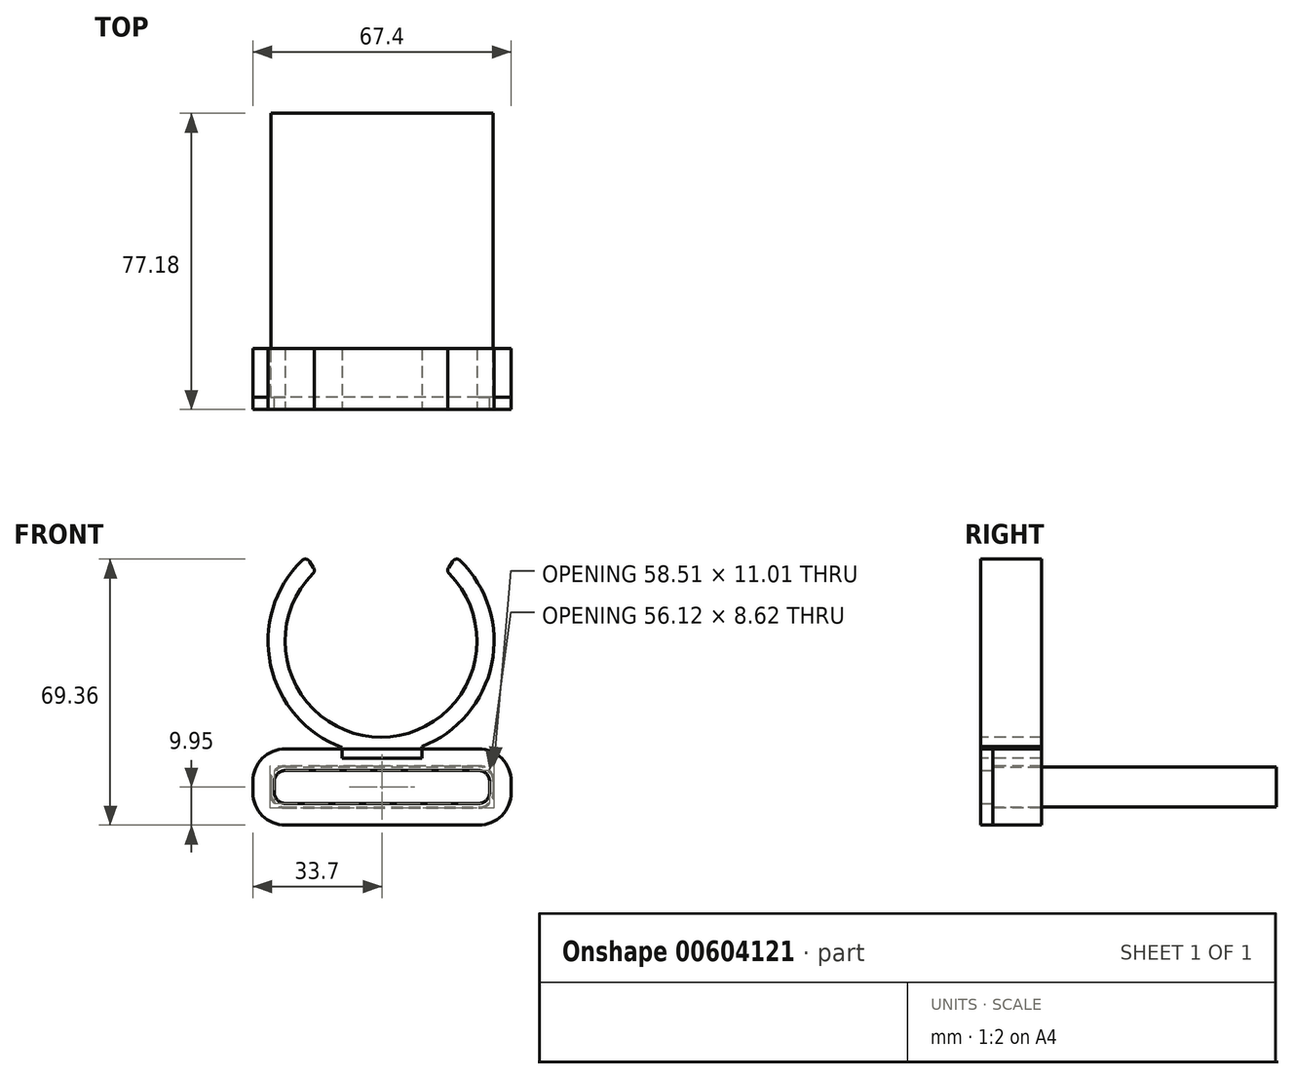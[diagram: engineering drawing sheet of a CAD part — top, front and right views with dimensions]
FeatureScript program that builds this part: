
annotation { "Feature Type Name" : "Feature", "Feature Type Description" : "" }
export const myFeature = defineFeature(function(context is Context, id is Id, definition is map)
    precondition{}
    {
        {
            var Q0;
            Q0=qCreatedBy(makeId("Top.planeOp"),FACE);
            var sketch = newSketch(context, id + "F0", { "sketchPlane" : qUnion([Q0])});
            skLineSegment(sketch, "E0.bottom", {"start": v(0, 0) * mm, "end": v(58, 0) * mm});
            skLineSegment(sketch, "E0.top", {"start": v(0, 74) * mm, "end": v(58, 74) * mm});
            skLineSegment(sketch, "E0.left", {"start": v(0, 0) * mm, "end": v(0, 74) * mm});
            skLineSegment(sketch, "E0.right", {"start": v(58, 0) * mm, "end": v(58, 74) * mm});
            skSolve(sketch);
        }
        {
            var Q0;
            Q0 = qSketchRegion(id + "F0", true);
            extrude(context, id + "F1", {"entities" : qUnion([Q0]), "depth" : 10.5 * mm, "offsetDistance" : 25.4 * mm});
        }
        {
            var Q0;
            Q0=makeQuery(id+"F1.opExtrude","CAP_EDGE",EDGE,{"disambiguationData":[OSD([sQuery(id+"F0.wireOp",EDGE,"E0.right")])],"isStart":true});
            var Q1;
            Q1=makeQuery(id+"F1.opExtrude","CAP_EDGE",EDGE,{"disambiguationData":[OSD([sQuery(id+"F0.wireOp",EDGE,"E0.right")])],"isStart":false});
            var Q2;
            Q2=makeQuery(id+"F1.opExtrude","CAP_EDGE",EDGE,{"disambiguationData":[OSD([sQuery(id+"F0.wireOp",EDGE,"E0.left")])],"isStart":true});
            var Q3;
            Q3=makeQuery(id+"F1.opExtrude","CAP_EDGE",EDGE,{"disambiguationData":[OSD([sQuery(id+"F0.wireOp",EDGE,"E0.left")])],"isStart":false});
            fillet(context, id + "F2", {"entities" : qUnion([Q0, Q1, Q2, Q3]), "radius" : 3.8 * mm, "tangentPropagation" : true, "allowEdgeOverflow" : false});
        }
        {
            var Q0;
            Q0=makeQuery(id+"F1.opExtrude","SWEPT_FACE",FACE,{"disambiguationData":[OSD([sQuery(id+"F0.wireOp",EDGE,"E0.bottom")])]});
            var sketch = newSketch(context, id + "F3", { "sketchPlane" : qUnion([Q0])});
            skArc(sketch, "E1.0", {"start": v(3.8, 10.75) * mm, "mid": v(0.94, 9.56) * mm, "end": v(-0.25, 6.7) * mm});
            skLineSegment(sketch, "E1.1", {"start": v(54.19, 10.75) * mm, "end": v(3.8, 10.75) * mm});
            skLineSegment(sketch, "E1.2", {"start": v(-0.25, 6.7) * mm, "end": v(-0.25, 3.81) * mm});
            skArc(sketch, "E1.3", {"start": v(58.25, 6.7) * mm, "mid": v(57.06, 9.56) * mm, "end": v(54.19, 10.75) * mm});
            skArc(sketch, "E1.4", {"start": v(-0.25, 3.81) * mm, "mid": v(0.94, 0.94) * mm, "end": v(3.81, -0.25) * mm});
            skLineSegment(sketch, "E1.5", {"start": v(3.81, -0.25) * mm, "end": v(54.19, -0.25) * mm});
            skArc(sketch, "E1.6", {"start": v(54.19, -0.25) * mm, "mid": v(57.06, 0.94) * mm, "end": v(58.25, 3.8) * mm});
            skLineSegment(sketch, "E1.7", {"start": v(58.25, 3.81) * mm, "end": v(58.25, 6.7) * mm});
            skArc(sketch, "E2.0", {"start": v(3.8, 15.2) * mm, "mid": v(-2.2, 12.7) * mm, "end": v(-4.7, 6.7) * mm});
            skLineSegment(sketch, "E2.1", {"start": v(54.19, 15.2) * mm, "end": v(3.8, 15.2) * mm});
            skLineSegment(sketch, "E2.2", {"start": v(-4.7, 6.7) * mm, "end": v(-4.7, 3.81) * mm});
            skArc(sketch, "E2.3", {"start": v(62.7, 6.7) * mm, "mid": v(60.2, 12.7) * mm, "end": v(54.19, 15.2) * mm});
            skArc(sketch, "E2.4", {"start": v(-4.7, 3.81) * mm, "mid": v(-2.2, -2.2) * mm, "end": v(3.81, -4.7) * mm});
            skLineSegment(sketch, "E2.5", {"start": v(3.81, -4.7) * mm, "end": v(54.19, -4.7) * mm});
            skArc(sketch, "E2.6", {"start": v(54.19, -4.7) * mm, "mid": v(60.2, -2.2) * mm, "end": v(62.7, 3.8) * mm});
            skLineSegment(sketch, "E2.7", {"start": v(62.7, 3.81) * mm, "end": v(62.7, 6.7) * mm});
            skSolve(sketch);
        }
        {
            var Q0;
            Q0 = qSketchRegion(id + "F3", true);
            extrude(context, id + "F4", {"entities" : qUnion([Q0]), "oppositeDirection" : true, "depth" : 12.7 * mm, "offsetDistance" : 25.4 * mm});
        }
        {
            var Q0;
            Q0=makeQuery(id+"F4.opExtrude","CAP_FACE",FACE,{"disambiguationData":[OSD([sQuery(id+"F3.wireOp",EDGE,"E1.0"),sQuery(id+"F3.wireOp",EDGE,"E1.1"),sQuery(id+"F3.wireOp",EDGE,"E1.2"),sQuery(id+"F3.wireOp",EDGE,"E1.3"),sQuery(id+"F3.wireOp",EDGE,"E1.4"),sQuery(id+"F3.wireOp",EDGE,"E1.5"),sQuery(id+"F3.wireOp",EDGE,"E1.6"),sQuery(id+"F3.wireOp",EDGE,"E1.7"),sQuery(id+"F3.wireOp",EDGE,"E2.0"),sQuery(id+"F3.wireOp",EDGE,"E2.1"),sQuery(id+"F3.wireOp",EDGE,"E2.2"),sQuery(id+"F3.wireOp",EDGE,"E2.3"),sQuery(id+"F3.wireOp",EDGE,"E2.4"),sQuery(id+"F3.wireOp",EDGE,"E2.5"),sQuery(id+"F3.wireOp",EDGE,"E2.6"),sQuery(id+"F3.wireOp",EDGE,"E2.7")])],"isStart":true});
            var sketch = newSketch(context, id + "F5", { "sketchPlane" : qUnion([Q0])});
            skLineSegment(sketch, "E3.0", {"start": v(54.19, 9.56) * mm, "end": v(3.8, 9.56) * mm});
            skArc(sketch, "E3.1", {"start": v(57.06, 6.7) * mm, "mid": v(56.22, 8.72) * mm, "end": v(54.19, 9.56) * mm});
            skArc(sketch, "E3.2", {"start": v(3.8, 9.56) * mm, "mid": v(1.78, 8.72) * mm, "end": v(0.94, 6.7) * mm});
            skLineSegment(sketch, "E3.3", {"start": v(57.06, 3.81) * mm, "end": v(57.06, 6.7) * mm});
            skLineSegment(sketch, "E3.4", {"start": v(0.94, 6.7) * mm, "end": v(0.94, 3.81) * mm});
            skArc(sketch, "E3.5", {"start": v(0.94, 3.81) * mm, "mid": v(1.78, 1.78) * mm, "end": v(3.81, 0.94) * mm});
            skLineSegment(sketch, "E3.6", {"start": v(3.81, 0.94) * mm, "end": v(54.19, 0.94) * mm});
            skArc(sketch, "E3.7", {"start": v(54.19, 0.94) * mm, "mid": v(56.22, 1.78) * mm, "end": v(57.06, 3.81) * mm});
            skSolve(sketch);
        }
        {
            var Q0;
            Q0=makeQuery(id+"F5.imprint","IMPRINT",FACE,{"disambiguationData":[TD([[makeQuery(id+"F5.imprint","IMPRINT",EDGE,{"derivedFrom":makeQuery(id+"F4.opExtrude","CAP_EDGE",EDGE,{"disambiguationData":[OSD([sQuery(id+"F3.wireOp",EDGE,"E1.0")])],"isStart":true})}),-1.0]])]});
            var Q1;
            Q1=makeQuery(id+"F5.imprint","IMPRINT",FACE,{"disambiguationData":[TD([[makeQuery(id+"F5.imprint","IMPRINT",EDGE,{"derivedFrom":sQuery(id+"F5.wireOp",EDGE,"E3.0")}),-1.0]])]});
            extrude(context, id + "F6", {"entities" : qUnion([Q0, Q1]), "depth" : 3.17 * mm, "offsetDistance" : 25.4 * mm});
        }
        {
            var Q0;
            Q0=makeQuery(id+"F6.opExtrude","CAP_FACE",FACE,{"disambiguationData":[OSD([sQuery(id+"F3.wireOp",EDGE,"E2.0"),sQuery(id+"F3.wireOp",EDGE,"E2.1"),sQuery(id+"F3.wireOp",EDGE,"E2.2"),sQuery(id+"F3.wireOp",EDGE,"E2.3"),sQuery(id+"F3.wireOp",EDGE,"E2.4"),sQuery(id+"F3.wireOp",EDGE,"E2.5"),sQuery(id+"F3.wireOp",EDGE,"E2.6"),sQuery(id+"F3.wireOp",EDGE,"E2.7"),sQuery(id+"F5.wireOp",EDGE,"E3.0"),sQuery(id+"F5.wireOp",EDGE,"E3.1"),sQuery(id+"F5.wireOp",EDGE,"E3.2"),sQuery(id+"F5.wireOp",EDGE,"E3.3"),sQuery(id+"F5.wireOp",EDGE,"E3.4"),sQuery(id+"F5.wireOp",EDGE,"E3.5"),sQuery(id+"F5.wireOp",EDGE,"E3.6"),sQuery(id+"F5.wireOp",EDGE,"E3.7")])],"isStart":false});
            var sketch = newSketch(context, id + "F7", { "sketchPlane" : qUnion([Q0])});
            skArc(sketch, "E4", {"start": v(10.98, 60.86) * mm, "mid": v(28.75, 18.23) * mm, "end": v(46.52, 60.86) * mm});
            skPoint(sketch, "E4.centerSnap0", {"position": v(28.75, 15.23) * mm});
            skArc(sketch, "E5", {"start": v(8.13, 64.3) * mm, "mid": v(28.75, 13.78) * mm, "end": v(49.37, 64.3) * mm});
            skLineSegment(sketch, "E6.bottom", {"start": v(39.39, 17.47) * mm, "end": v(18.61, 17.47) * mm});
            skLineSegment(sketch, "E6.top", {"start": v(39.39, 12.8) * mm, "end": v(18.61, 12.8) * mm});
            skLineSegment(sketch, "E6.left", {"start": v(39.39, 17.47) * mm, "end": v(39.39, 12.8) * mm});
            skLineSegment(sketch, "E6.right", {"start": v(18.61, 17.47) * mm, "end": v(18.61, 12.8) * mm});
            skPoint(sketch, "E6.middle", {"position": v(29, 15.2) * mm});
            skLineSegment(sketch, "E7", {"start": v(11.14, 62.44) * mm, "end": v(10.09, 64.08) * mm});
            skLineSegment(sketch, "E8", {"start": v(28.75, 15.23) * mm, "end": v(28.75, 43.25) * mm, "construction": true});
            skLineSegment(sketch, "E9.MirrorCS", {"start": v(46.35, 62.44) * mm, "end": v(47.41, 64.08) * mm});
            skPoint(sketch, "E10.MirrorP", {"position": v(28.5, 15.2) * mm});
            skPoint(sketch, "E11.visualSharp", {"position": v(9.26, 65.35) * mm});
            skArc(sketch, "E11.filletArc", {"start": v(10.09, 64.08) * mm, "mid": v(9.16, 64.65) * mm, "end": v(8.13, 64.3) * mm});
            skPoint(sketch, "E12.visualSharp", {"position": v(11.7, 61.57) * mm});
            skArc(sketch, "E12.filletArc", {"start": v(10.98, 60.86) * mm, "mid": v(11.34, 61.62) * mm, "end": v(11.14, 62.44) * mm});
            skPoint(sketch, "E13.visualSharp", {"position": v(45.79, 61.57) * mm});
            skArc(sketch, "E13.filletArc", {"start": v(46.35, 62.44) * mm, "mid": v(46.16, 61.62) * mm, "end": v(46.52, 60.86) * mm});
            skArc(sketch, "E14.filletArc", {"start": v(49.37, 64.3) * mm, "mid": v(48.34, 64.65) * mm, "end": v(47.41, 64.08) * mm});
            skSolve(sketch);
        }
        {
            var Q0;
            Q0 = qSketchRegion(id + "F7", true);
            extrude(context, id + "F8", {"entities" : qUnion([Q0]), "oppositeDirection" : true, "depth" : 15.88 * mm, "offsetDistance" : 25.4 * mm});
        }
    });
